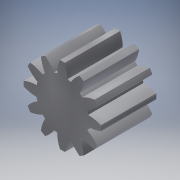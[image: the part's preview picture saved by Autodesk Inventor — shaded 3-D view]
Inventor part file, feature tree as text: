
AUTODESK INVENTOR PART (.ipt)
format: ipt  version: 2019 (Build 230136000, 136)  size: 199,168 bytes
history: native  units: mm (DEFAULTED — no unit token found)
features: plane x3, other x3, sketch x2, extrude x1
ambient origin geometry x8: Origin, YZ Plane, XZ Plane, XY Plane, X Axis, Y Axis, Z Axis, Center Point
bodies: Solid1 (feature_tree)
feature tree (9):
  extrude  "Extrusion1"  Depth=2.0mm TaperAngle=0.0deg
  plane  "Work Plane2"
  plane  "Work Plane8"
  plane  "Work Plane9"
  other  "Spur Gear"
  sketch  "Sketch1"  dims[d0=2.799202mm d1=2.0mm d2=0.0mm]
  sketch  "Sketch2"  dims[d3=2.39mm d4=10.0mm d5=0.0mm d16=5.975mm d17=0.0mm d34=15.0deg d39=0.0mm d41=0.0mm d43=5.975mm d46=5.975mm d47=0.0mm d48=0.0mm]
  other  "Srf1"
  other  "Pitch Diameter"
